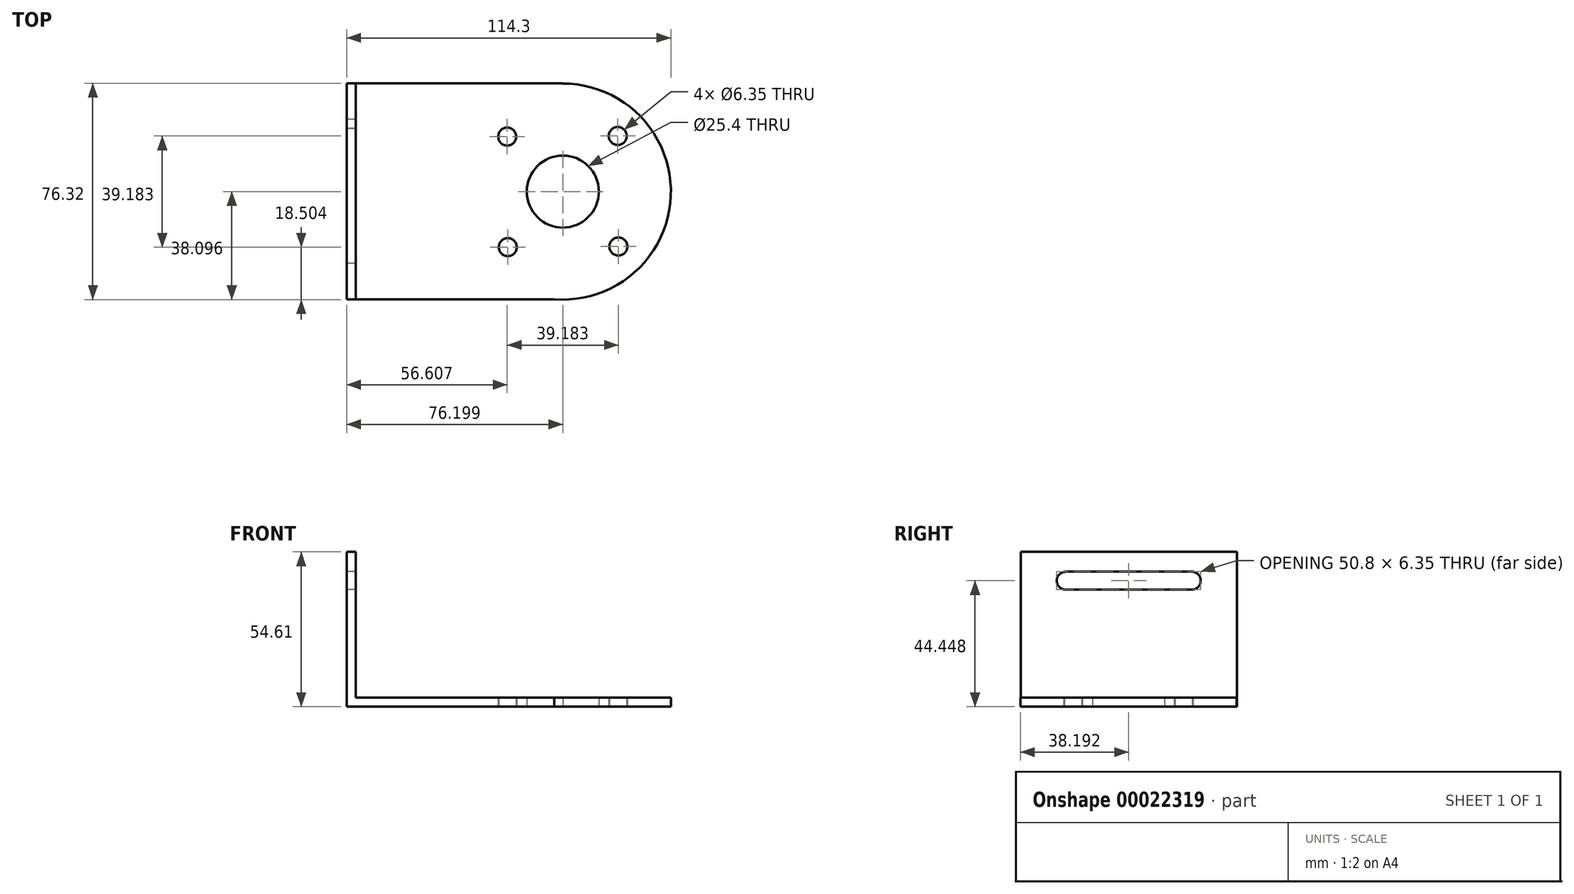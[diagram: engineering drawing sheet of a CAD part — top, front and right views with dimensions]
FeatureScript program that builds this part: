
annotation { "Feature Type Name" : "Feature", "Feature Type Description" : "" }
export const myFeature = defineFeature(function(context is Context, id is Id, definition is map)
    precondition{}
    {
        {
            var Q0;
            Q0=qCreatedBy(makeId("Top.planeOp"),FACE);
            var sketch = newSketch(context, id + "F0", { "sketchPlane" : qUnion([Q0])});
            skLineSegment(sketch, "E0.bottom", {"start": v(-53.2, 53.9) * mm, "end": v(23, 53.9) * mm});
            skLineSegment(sketch, "E0.top", {"start": v(-53.2, -22.3) * mm, "end": v(23, -22.3) * mm});
            skLineSegment(sketch, "E0.left", {"start": v(-53.2, 53.9) * mm, "end": v(-53.2, -22.3) * mm});
            skLineSegment(sketch, "E0.right", {"start": v(23, 53.9) * mm, "end": v(23, -22.3) * mm});
            skCircle(sketch, "E1", {"center": v(23, 15.68) * mm, "radius": 38.1 * mm});
            skCircle(sketch, "E2", {"center": v(23, 15.68) * mm, "radius": 12.7 * mm});
            skCircle(sketch, "E3", {"center": v(3.4, 35.07) * mm, "radius": 3.18 * mm});
            skCircle(sketch, "E4.1.0", {"center": v(3.6, -3.92) * mm, "radius": 3.18 * mm});
            skCircle(sketch, "E4.2.0", {"center": v(42.6, -3.71) * mm, "radius": 3.18 * mm});
            skCircle(sketch, "E4.3.0", {"center": v(42.39, 35.27) * mm, "radius": 3.18 * mm});
            skSolve(sketch);
        }
        {
            var Q0;
            Q0 = qSketchRegion(id + "F0", true);
            extrude(context, id + "F1", {"entities" : qUnion([Q0]), "depth" : 3.17 * mm});
        }
        {
            var Q0;
            Q0=makeQuery(id+"F1.opExtrude","CAP_FACE",FACE,{"disambiguationData":[OSD([sQuery(id+"F0.wireOp",EDGE,"E0.bottom"),sQuery(id+"F0.wireOp",EDGE,"E0.top"),sQuery(id+"F0.wireOp",EDGE,"E0.left"),sQuery(id+"F0.wireOp",EDGE,"E0.right"),sQuery(id+"F0.wireOp",EDGE,"E1"),sQuery(id+"F0.wireOp",EDGE,"E2"),sQuery(id+"F0.wireOp",EDGE,"E3"),sQuery(id+"F0.wireOp",EDGE,"E4.1.0"),sQuery(id+"F0.wireOp",EDGE,"E4.2.0"),sQuery(id+"F0.wireOp",EDGE,"E4.3.0")])],"isStart":false});
            var sketch = newSketch(context, id + "F2", { "sketchPlane" : qUnion([Q0])});
            skLineSegment(sketch, "E5.bottom", {"start": v(-53.2, 53.9) * mm, "end": v(-50.03, 53.9) * mm});
            skLineSegment(sketch, "E5.top", {"start": v(-53.2, -22.3) * mm, "end": v(-50.03, -22.3) * mm});
            skLineSegment(sketch, "E5.left", {"start": v(-53.2, 53.9) * mm, "end": v(-53.2, -22.3) * mm});
            skLineSegment(sketch, "E5.right", {"start": v(-50.03, 53.9) * mm, "end": v(-50.03, -22.3) * mm});
            skSolve(sketch);
        }
        {
            var Q0;
            Q0 = qSketchRegion(id + "F2", true);
            extrude(context, id + "F3", {"entities" : qUnion([Q0]), "operationType" : NewBodyOperationType.ADD, "depth" : 51.43 * mm});
        }
        {
            var Q0;
            Q0=makeQuery(id+"F3.boolean.opBoolean","MERGE",FACE,{"derivedFrom":[makeQuery(id+"F1.opExtrude","SWEPT_FACE",FACE,{"disambiguationData":[OSD([sQuery(id+"F0.wireOp",EDGE,"E0.left")])]}),makeQuery(id+"F3.opExtrude","SWEPT_FACE",FACE,{"disambiguationData":[OSD([sQuery(id+"F2.wireOp",EDGE,"E5.left")])]})]});
            var sketch = newSketch(context, id + "F4", { "sketchPlane" : qUnion([Q0])});
            skLineSegment(sketch, "E6.left", {"start": v(-38, 47.62) * mm, "end": v(-38, 41.28) * mm});
            skLineSegment(sketch, "E6.right", {"start": v(6.45, 47.62) * mm, "end": v(6.45, 41.27) * mm});
            skCircle(sketch, "E7", {"center": v(-38, 44.45) * mm, "radius": 3.18 * mm});
            skCircle(sketch, "E8", {"center": v(6.45, 44.45) * mm, "radius": 3.18 * mm});
            skLineSegment(sketch, "E9", {"start": v(-15.8, 54.6) * mm, "end": v(-15.8, 0) * mm, "construction": true});
            skLineSegment(sketch, "E10", {"start": v(-15.68, 47.48) * mm, "end": v(-15.68, 41.42) * mm, "construction": true});
            skLineSegment(sketch, "E11.bottom", {"start": v(-38, 47.62) * mm, "end": v(6.45, 47.62) * mm});
            skLineSegment(sketch, "E11.top", {"start": v(-38, 41.27) * mm, "end": v(6.45, 41.27) * mm});
            skLineSegment(sketch, "E11.left", {"start": v(-38, 47.62) * mm, "end": v(-38, 41.27) * mm});
            skSolve(sketch);
        }
        {
            var Q0;
            Q0 = qSketchRegion(id + "F4", true);
            var Q1;
            {var subQ0=sQuery(id+"F4.wireOp",EDGE,"E6.right");Q1=makeQuery(id+"F4.imprint","IMPRINT",FACE,{"disambiguationData":[TD([[makeQuery(id+"F4.imprint","IMPRINT",EDGE,{"derivedFrom":subQ0}),-1.0]])]});}
            extrude(context, id + "F5", {"entities" : qUnion([Q0, Q1]), "operationType" : NewBodyOperationType.REMOVE, "endBound" : BoundingType.UP_TO_NEXT, "oppositeDirection" : true, "depth" : 25.4 * mm});
        }
    });
